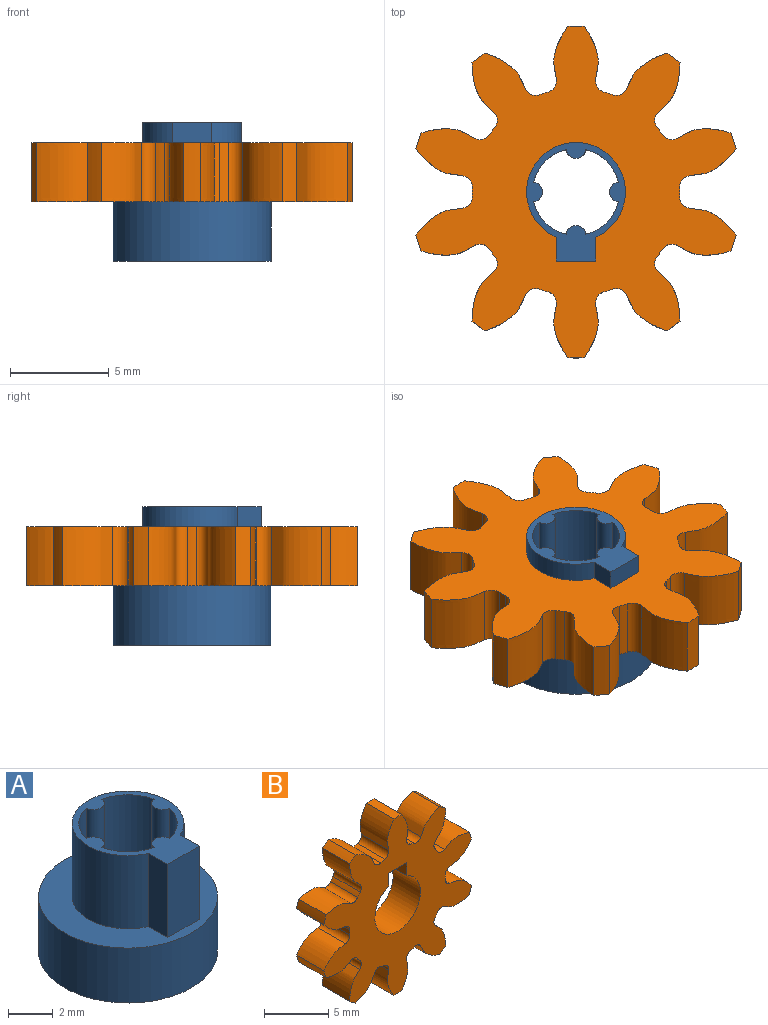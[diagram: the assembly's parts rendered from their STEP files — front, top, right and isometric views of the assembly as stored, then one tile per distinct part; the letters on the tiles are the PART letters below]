
ASSEMBLY  parts=2 mates=1
PART A: 18 faces, bbox 8x8x7 mm
  f0: cylinder r=2.2mm len=5mm, axis (0,0,-1), area 12.3mm2, adj f1,f7,f15,f17
  f1: cylinder r=0.5mm len=5mm, axis (0,0,-1), area 7.3mm2, adj f0,f2,f15,f17
  f2: cylinder r=2.2mm len=5mm, axis (0,0,-1), area 12.3mm2, adj f1,f3,f15,f17
  f3: cylinder r=0.5mm len=5mm, axis (0,0,-1), area 7.3mm2, adj f2,f4,f15,f17
  f4: cylinder r=2.2mm len=5mm, axis (0,0,-1), area 12.3mm2, adj f3,f5,f15,f17
  f5: cylinder r=0.5mm len=5mm, axis (0,0,-1), area 7.3mm2, adj f4,f6,f15,f17
  f6: cylinder r=2.2mm len=5mm, axis (0,0,-1), area 12.3mm2, adj f5,f7,f15,f17
  f7: cylinder r=0.5mm len=5mm, axis (0,0,-1), area 7.3mm2, adj f0,f6,f15,f17
  f8: cylinder r=4mm len=8mm, axis (0,0,-1), area 75.4mm2, adj f9,f10
  f9: plane 8x8mm, normal (0,0,1), area 28.5mm2, adj f8,f11,f12,f13,f14
  f10: plane 8x8mm, normal (0,0,-1), area 17.1mm2, adj f8,f16
  f11: cylinder r=2.5mm len=5mm, axis (0,0,-1), area 54.6mm2, adj f9,f12,f14,f15
  f12: plane 4x1.21mm, normal (-1,0,0), area 4.8mm2, adj f9,f11,f13,f15
  f13: plane 4x2mm, normal (0,-1,0), area 8mm2, adj f9,f12,f14,f15
  f14: plane 4x1.21mm, normal (1,0,0), area 4.8mm2, adj f9,f11,f13,f15
  f15: plane 6x5mm, normal (0,0,1), area 8.1mm2, adj f0,f1,f2,f3,f4,f5,f6,f7
  f16: cylinder r=3.25mm len=6.5mm, axis (0,0,1), area 40.8mm2, adj f10,f17
  f17: plane 6.5x6.5mm, normal (0,0,-1), area 19.5mm2, adj f0,f1,f2,f3,f4,f5,f6,f7
PART B: 66 faces, bbox 16.2x3x16.8 mm
  f0: cylinder r=8.4mm len=3mm, axis (0,1,0), area 2.5mm2, adj f9,f15,f56,f63
  f1: cylinder r=8.4mm len=3mm, axis (0,1,0), area 2.5mm2, adj f9,f15,f16,f58
  f2: cylinder r=8.4mm len=3mm, axis (0,1,0), area 2.5mm2, adj f9,f15,f46,f53
  f3: cylinder r=8.4mm len=3mm, axis (0,1,0), area 2.5mm2, adj f9,f15,f48,f61
  f4: cylinder r=8.4mm len=3mm, axis (0,1,0), area 2.5mm2, adj f9,f15,f36,f43
  f5: cylinder r=8.4mm len=3mm, axis (0,1,0), area 2.5mm2, adj f9,f15,f31,f38
  f6: cylinder r=8.4mm len=3mm, axis (0,1,0), area 2.5mm2, adj f9,f15,f26,f33
  f7: cylinder r=8.4mm len=3mm, axis (0,1,0), area 2.5mm2, adj f9,f15,f28,f51
  f8: cylinder r=8.4mm len=3mm, axis (0,1,0), area 2.5mm2, adj f9,f15,f23,f41
  f9: plane 16.83x16.25mm, normal (0,-1,0), area 125.5mm2, adj f0,f1,f2,f3,f4,f5,f6,f7
  f10: plane 3x1.21mm, normal (-1,0,0), area 3.6mm2, adj f9,f11,f13,f15
  f11: cylinder r=2.5mm len=5mm, axis (0,1,0), area 41mm2, adj f9,f10,f12,f15
  f12: plane 3x1.21mm, normal (1,0,0), area 3.6mm2, adj f9,f11,f13,f15
  f13: plane 3x2mm, normal (0,0,-1), area 6mm2, adj f9,f10,f12,f15
  f14: cylinder r=8.4mm len=3mm, axis (0,1,0), area 2.5mm2, adj f9,f15,f18,f21
  f15: plane 16.83x16.25mm, normal (0,1,0), area 125.5mm2, adj f0,f1,f2,f3,f4,f5,f6,f7
  f16: extruded ~3x2.37mm, area 8.5mm2, adj f1,f9,f15,f19
  f17: cylinder r=5.25mm len=3mm, axis (0,1,0), area 1.3mm2, adj f9,f15,f19,f20
  f18: extruded ~3x2.37mm, area 8.5mm2, adj f9,f14,f15,f20
  f19: cylinder r=0.58mm len=3mm, axis (0,1,0), area 2.5mm2, adj f9,f15,f16,f17
  f20: cylinder r=0.58mm len=3mm, axis (0,1,0), area 2.5mm2, adj f9,f15,f17,f18
  f21: extruded ~3x2.73mm, area 8.5mm2, adj f9,f14,f15,f24
  f22: cylinder r=5.25mm len=3mm, axis (0,1,0), area 1.3mm2, adj f9,f15,f24,f25
  f23: extruded ~3x2.51mm, area 8.5mm2, adj f8,f9,f15,f25
  f24: cylinder r=0.58mm len=3mm, axis (0,1,0), area 2.5mm2, adj f9,f15,f21,f22
  f25: cylinder r=0.58mm len=3mm, axis (0,1,0), area 2.5mm2, adj f9,f15,f22,f23
  f26: extruded ~3x2.37mm, area 8.5mm2, adj f6,f9,f15,f29
  f27: cylinder r=5.25mm len=3mm, axis (0,1,0), area 1.3mm2, adj f9,f15,f29,f30
  f28: extruded ~3x2.37mm, area 8.5mm2, adj f7,f9,f15,f30
  f29: cylinder r=0.58mm len=3mm, axis (0,1,0), area 2.5mm2, adj f9,f15,f26,f27
  f30: cylinder r=0.58mm len=3mm, axis (0,1,0), area 2.5mm2, adj f9,f15,f27,f28
  f31: extruded ~3x2.51mm, area 8.5mm2, adj f5,f9,f15,f34
  f32: cylinder r=5.25mm len=3mm, axis (0,1,0), area 1.3mm2, adj f9,f15,f34,f35
  f33: extruded ~3x2.73mm, area 8.5mm2, adj f6,f9,f15,f35
  f34: cylinder r=0.58mm len=3mm, axis (0,1,0), area 2.5mm2, adj f9,f15,f31,f32
  f35: cylinder r=0.58mm len=3mm, axis (0,1,0), area 2.5mm2, adj f9,f15,f32,f33
  f36: extruded ~3x2.68mm, area 8.5mm2, adj f4,f9,f15,f39
  f37: cylinder r=5.25mm len=3mm, axis (0,1,0), area 1.3mm2, adj f9,f15,f39,f40
  f38: extruded ~3x2.05mm, area 8.5mm2, adj f5,f9,f15,f40
  f39: cylinder r=0.58mm len=3mm, axis (0,1,0), area 2.5mm2, adj f9,f15,f36,f37
  f40: cylinder r=0.58mm len=3mm, axis (0,1,0), area 2.5mm2, adj f9,f15,f37,f38
  f41: extruded ~3x2.05mm, area 8.5mm2, adj f8,f9,f15,f44
  f42: cylinder r=5.25mm len=3mm, axis (0,1,0), area 1.3mm2, adj f9,f15,f44,f45
  f43: extruded ~3x2.68mm, area 8.5mm2, adj f4,f9,f15,f45
  f44: cylinder r=0.58mm len=3mm, axis (0,1,0), area 2.5mm2, adj f9,f15,f41,f42
  f45: cylinder r=0.58mm len=3mm, axis (0,1,0), area 2.5mm2, adj f9,f15,f42,f43
  f46: extruded ~3x2.05mm, area 8.5mm2, adj f2,f9,f15,f49
  f47: cylinder r=5.25mm len=3mm, axis (0,1,0), area 1.3mm2, adj f9,f15,f49,f50
  f48: extruded ~3x2.68mm, area 8.5mm2, adj f3,f9,f15,f50
  f49: cylinder r=0.58mm len=3mm, axis (0,1,0), area 2.5mm2, adj f9,f15,f46,f47
  f50: cylinder r=0.58mm len=3mm, axis (0,1,0), area 2.5mm2, adj f9,f15,f47,f48
  f51: extruded ~3x2.73mm, area 8.5mm2, adj f7,f9,f15,f54
  f52: cylinder r=5.25mm len=3mm, axis (0,1,0), area 1.3mm2, adj f9,f15,f54,f55
  f53: extruded ~3x2.51mm, area 8.5mm2, adj f2,f9,f15,f55
  f54: cylinder r=0.58mm len=3mm, axis (0,1,0), area 2.5mm2, adj f9,f15,f51,f52
  f55: cylinder r=0.58mm len=3mm, axis (0,1,0), area 2.5mm2, adj f9,f15,f52,f53
  f56: extruded ~3x2.51mm, area 8.5mm2, adj f0,f9,f15,f59
  f57: cylinder r=5.25mm len=3mm, axis (0,1,0), area 1.3mm2, adj f9,f15,f59,f60
  f58: extruded ~3x2.73mm, area 8.5mm2, adj f1,f9,f15,f60
  f59: cylinder r=0.58mm len=3mm, axis (0,1,0), area 2.5mm2, adj f9,f15,f56,f57
  f60: cylinder r=0.58mm len=3mm, axis (0,1,0), area 2.5mm2, adj f9,f15,f57,f58
  f61: extruded ~3x2.68mm, area 8.5mm2, adj f3,f9,f15,f64
  f62: cylinder r=5.25mm len=3mm, axis (0,1,0), area 1.3mm2, adj f9,f15,f64,f65
  f63: extruded ~3x2.05mm, area 8.5mm2, adj f0,f9,f15,f65
  f64: cylinder r=0.58mm len=3mm, axis (0,1,0), area 2.5mm2, adj f9,f15,f61,f62
  f65: cylinder r=0.58mm len=3mm, axis (0,1,0), area 2.5mm2, adj f9,f15,f62,f63
PLACE A at identity fixed
PLACE B rot(axis=(1,0,0),90deg) t=(0,0,20)mm
MATE fastened B.f13 <-> A.f13  axis (0,1,0) through (-1,-3.5,17)mm
